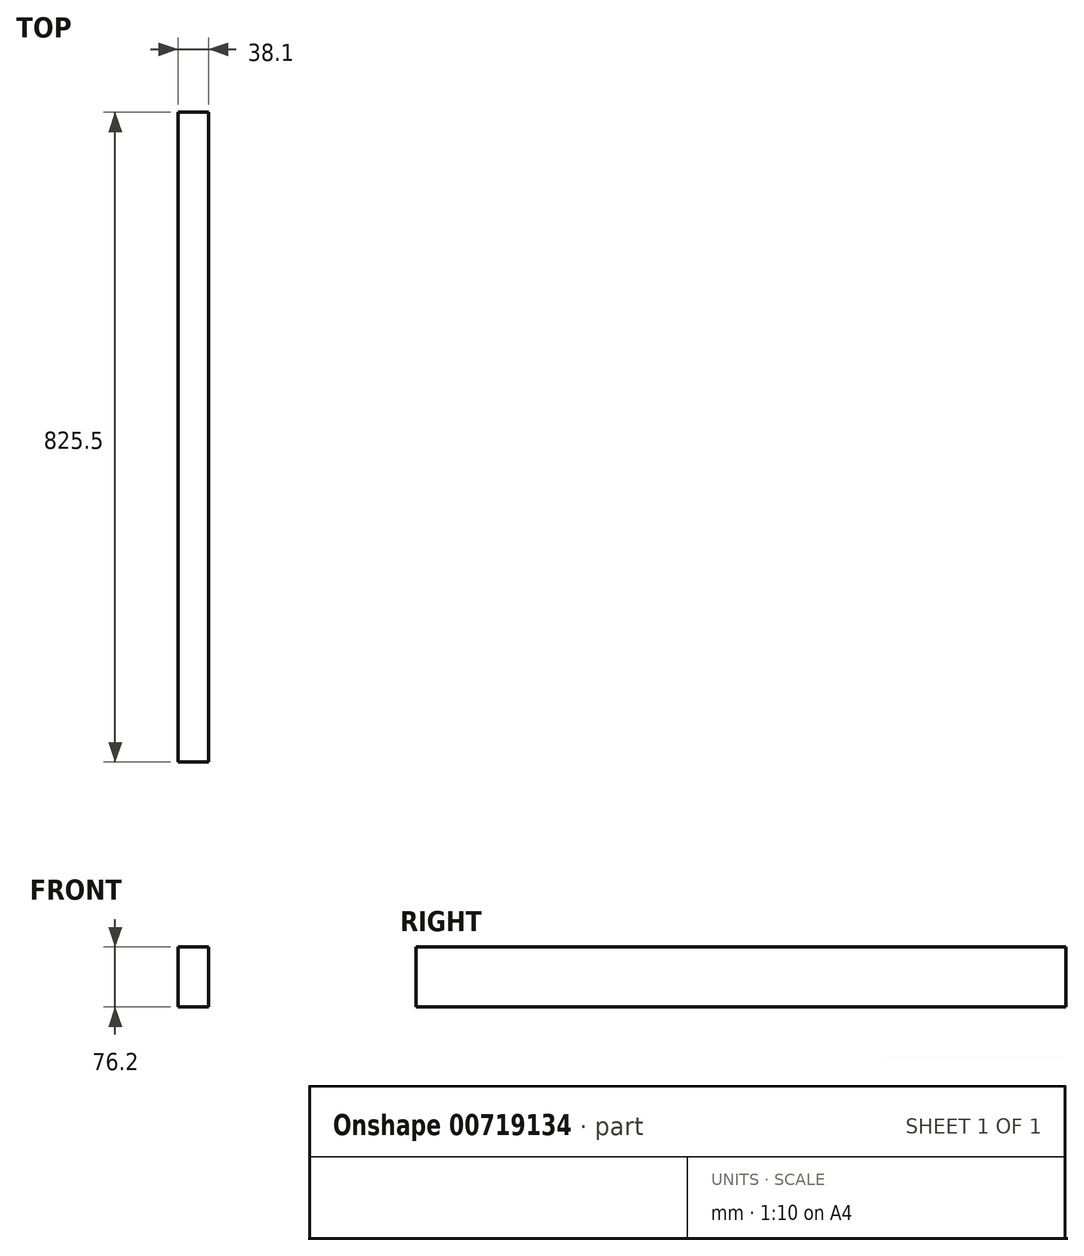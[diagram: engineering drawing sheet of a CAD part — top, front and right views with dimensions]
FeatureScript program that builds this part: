
annotation { "Feature Type Name" : "Feature", "Feature Type Description" : "" }
export const myFeature = defineFeature(function(context is Context, id is Id, definition is map)
    precondition{}
    {
        {
            var Q0;
            Q0=qCreatedBy(makeId("Front.planeOp"),FACE);
            var sketch = newSketch(context, id + "F0", { "sketchPlane" : qUnion([Q0])});
            skLineSegment(sketch, "E0.bottom", {"start": v(0, 0) * mm, "end": v(-38.1, 0) * mm});
            skLineSegment(sketch, "E0.top", {"start": v(0, 76.2) * mm, "end": v(-38.1, 76.2) * mm});
            skLineSegment(sketch, "E0.left", {"start": v(0, 0) * mm, "end": v(0, 76.2) * mm});
            skLineSegment(sketch, "E0.right", {"start": v(-38.1, 0) * mm, "end": v(-38.1, 76.2) * mm});
            skSolve(sketch);
        }
        {
            var Q0;
            Q0 = qSketchRegion(id + "F0", true);
            extrude(context, id + "F1", {"entities" : qUnion([Q0]), "depth" : 825.5 * mm, "offsetDistance" : 25.4 * mm});
        }
    });
